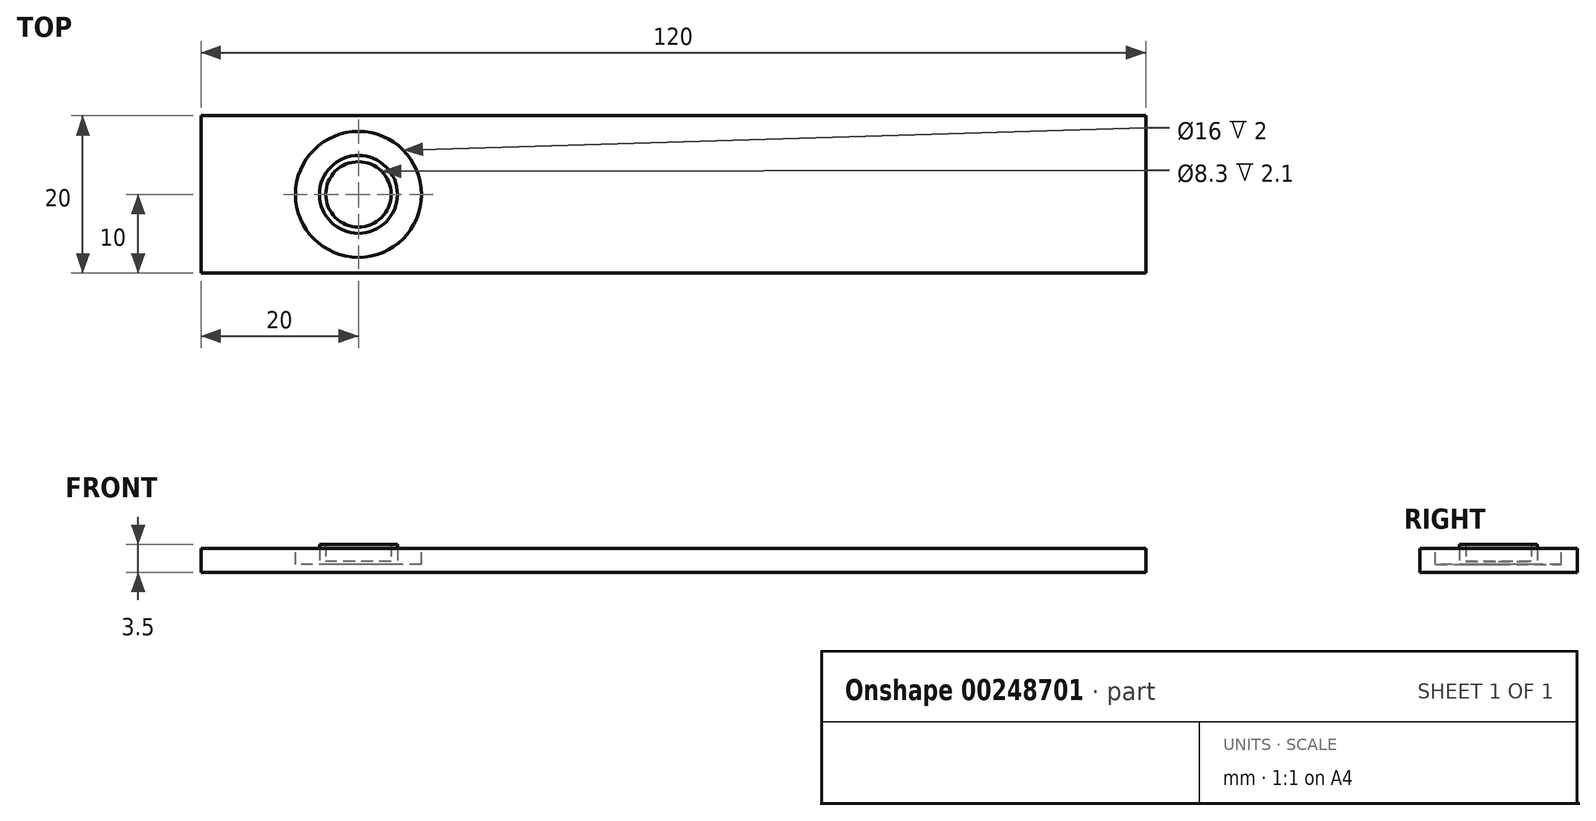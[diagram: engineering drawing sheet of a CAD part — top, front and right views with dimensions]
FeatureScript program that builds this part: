
annotation { "Feature Type Name" : "Feature", "Feature Type Description" : "" }
export const myFeature = defineFeature(function(context is Context, id is Id, definition is map)
    precondition{}
    {
        {
            var Q0;
            Q0=qCreatedBy(makeId("Top.planeOp"),FACE);
            var sketch = newSketch(context, id + "F0", { "sketchPlane" : qUnion([Q0])});
            skLineSegment(sketch, "E0.bottom", {"start": v(-60, 10) * mm, "end": v(60, 10) * mm});
            skLineSegment(sketch, "E0.top", {"start": v(-60, -10) * mm, "end": v(60, -10) * mm});
            skLineSegment(sketch, "E0.left", {"start": v(-60, 10) * mm, "end": v(-60, -10) * mm});
            skLineSegment(sketch, "E0.right", {"start": v(60, 10) * mm, "end": v(60, -10) * mm});
            skPoint(sketch, "E0.middle", {"position": v(0, 0) * mm});
            skPoint(sketch, "E1.centerSnap0", {"position": v(-60, 0) * mm});
            skSolve(sketch);
        }
        {
            var Q0;
            Q0 = qSketchRegion(id + "F0", true);
            extrude(context, id + "F1", {"entities" : qUnion([Q0]), "depth" : 3 * mm});
        }
        {
            var Q0;
            Q0=makeQuery(id+"F1.opExtrude","CAP_FACE",FACE,{"disambiguationData":[OSD([sQuery(id+"F0.wireOp",EDGE,"E0.bottom"),sQuery(id+"F0.wireOp",EDGE,"E0.top"),sQuery(id+"F0.wireOp",EDGE,"E0.left"),sQuery(id+"F0.wireOp",EDGE,"E0.right")])],"isStart":false});
            var sketch = newSketch(context, id + "F2", { "sketchPlane" : qUnion([Q0])});
            skCircle(sketch, "E2", {"center": v(-40, 0) * mm, "radius": 8 * mm});
            skPoint(sketch, "E2.centerSnap0", {"position": v(-60, 0) * mm});
            skSolve(sketch);
        }
        {
            var Q0;
            Q0 = qSketchRegion(id + "F2", true);
            extrude(context, id + "F3", {"entities" : qUnion([Q0]), "operationType" : NewBodyOperationType.REMOVE, "oppositeDirection" : true, "depth" : 2 * mm});
        }
        {
            var Q0;
            Q0=makeQuery(id+"F3.boolean.opBoolean","COPY",FACE,{"derivedFrom":makeQuery(id+"F3.opExtrude","CAP_FACE",FACE,{"disambiguationData":[OSD([sQuery(id+"F2.wireOp",EDGE,"E2")])],"isStart":false})});
            var sketch = newSketch(context, id + "F4", { "sketchPlane" : qUnion([Q0])});
            skCircle(sketch, "E3", {"center": v(-40, 0) * mm, "radius": 4.15 * mm});
            skCircle(sketch, "E4", {"center": v(-40, 0) * mm, "radius": 4.95 * mm});
            skSolve(sketch);
        }
        {
            var Q0;
            Q0 = qSketchRegion(id + "F4", true);
            extrude(context, id + "F5", {"entities" : qUnion([Q0]), "operationType" : NewBodyOperationType.ADD, "depth" : 2.5 * mm});
        }
        {
            var Q0;
            Q0=makeQuery(id+"F5.boolean.opBoolean","SPLIT",FACE,{"disambiguationData":[TD([makeQuery(id+"F5.opExtrude","SWEPT_FACE",FACE,{"disambiguationData":[OSD([sQuery(id+"F4.wireOp",EDGE,"E3")])]})])],"derivedFrom":makeQuery(id+"F3.boolean.opBoolean","COPY",FACE,{"derivedFrom":makeQuery(id+"F3.opExtrude","CAP_FACE",FACE,{"disambiguationData":[OSD([sQuery(id+"F2.wireOp",EDGE,"E2")])],"isStart":false})})});
            extrude(context, id + "F6", {"entities" : qUnion([Q0]), "operationType" : NewBodyOperationType.ADD, "depth" : 0.4 * mm});
        }
    });
